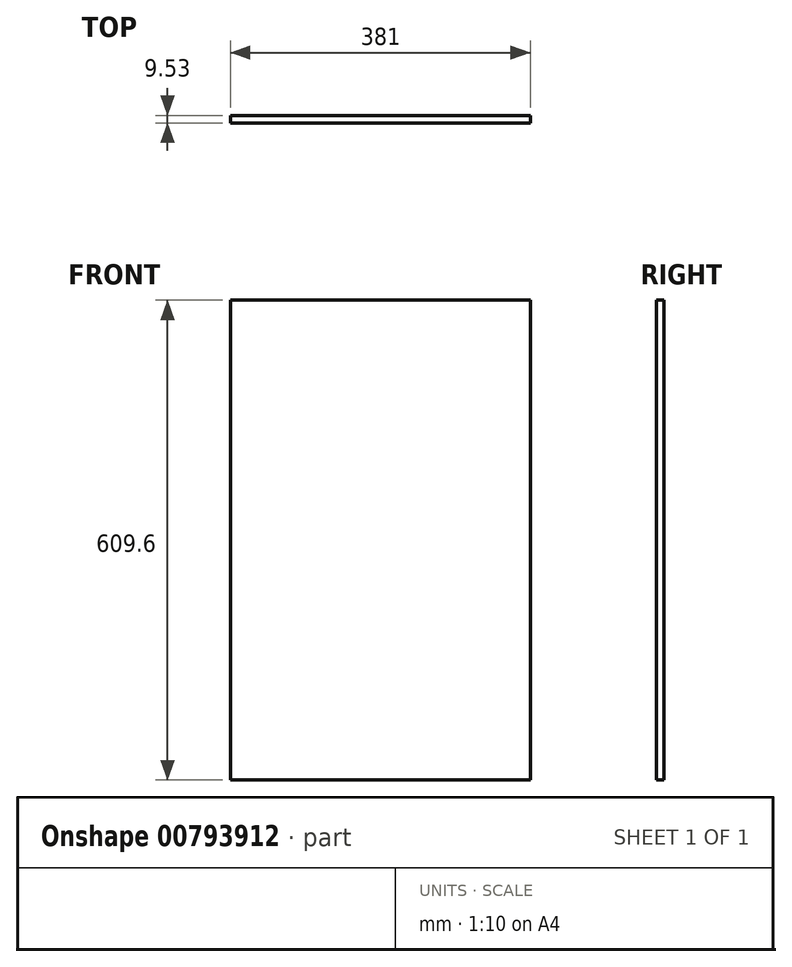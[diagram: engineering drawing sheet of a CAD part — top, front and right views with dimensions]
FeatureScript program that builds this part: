
annotation { "Feature Type Name" : "Feature", "Feature Type Description" : "" }
export const myFeature = defineFeature(function(context is Context, id is Id, definition is map)
    precondition{}
    {
        {
            var Q0;
            Q0=qCreatedBy(makeId("Front.planeOp"),FACE);
            var sketch = newSketch(context, id + "F0", { "sketchPlane" : qUnion([Q0])});
            skLineSegment(sketch, "E0.bottom", {"start": v(190.5, 304.8) * mm, "end": v(-190.5, 304.8) * mm});
            skLineSegment(sketch, "E0.top", {"start": v(190.5, -304.8) * mm, "end": v(-190.5, -304.8) * mm});
            skLineSegment(sketch, "E0.left", {"start": v(190.5, 304.8) * mm, "end": v(190.5, -304.8) * mm});
            skLineSegment(sketch, "E0.right", {"start": v(-190.5, 304.8) * mm, "end": v(-190.5, -304.8) * mm});
            skPoint(sketch, "E0.middle", {"position": v(0, 0) * mm});
            skSolve(sketch);
        }
        {
            var Q0;
            Q0=qSketchRegion(id+"F0",true);
            extrude(context, id + "F1", {"entities" : qUnion([Q0]), "oppositeDirection" : true, "depth" : 9.52 * mm, "offsetDistance" : 25.4 * mm});
        }
    });
